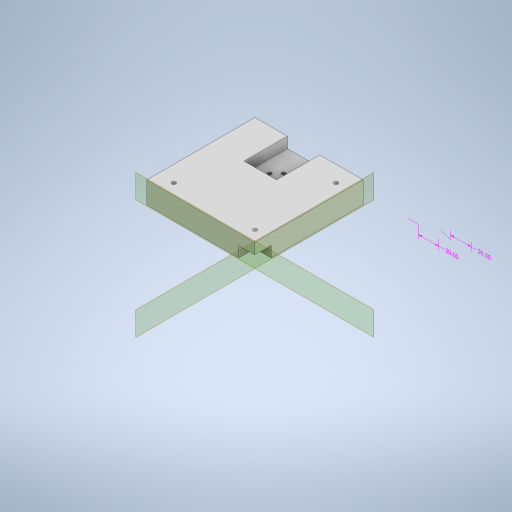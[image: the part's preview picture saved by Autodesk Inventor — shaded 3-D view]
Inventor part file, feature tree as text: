
AUTODESK INVENTOR PART (.ipt)
format: ipt  version: 2023 (Build 270158000, 158)  size: 370,176 bytes
history: native  units: mm
features: sketch x8, extrude x5, other x4, hole x3, plane x2, split x2
ambient origin geometry x8: Origin, YZ Plane, XZ Plane, XY Plane, X Axis, Y Axis, Z Axis, Center Point
bodies: Body1 (feature_tree)
feature tree (24):
  other  "Sólido1"
  other  "Anotaciones"
  extrude  "Extrusión1"  Depth=200.0mm
  extrude  "Extrusión2"  Depth=10.0mm TaperAngle=0.0deg
  extrude  "Extrusión3"  Depth=20.0mm
  hole  "Agujero1"  [1 undecoded]
  extrude  "Extrusión4"  Depth=10.0mm
  plane  "Plano de trabajo1"
  plane  "Plano de trabajo2"
  hole  "Agujero2"  [1 undecoded]
  extrude  "Extrusión5"  Depth=10.0mm TaperAngle=0.0deg
  hole  "Agujero3"  [1 undecoded]
  split  "Dividir1"
  split  "Dividir2"
  sketch  "Boceto1"  dims[d0=200.0mm d1=200.0mm]
  sketch  "Boceto2"  dims[d2=20.0mm d3=0.0mm]
  sketch  "Boceto3"  dims[d4=20.0mm d5=20.0mm d6=30.0mm d7=30.0mm d8=20.0mm d9=35.0mm d10=35.0mm d11=60.0mm d12=10.0mm d13=0.0mm]
  sketch  "Boceto4"  dims[d14=20.0mm d15=0.0mm]
  sketch  "Boceto5"  dims[d16=3.5mm d18=1.75mm d19=1.75mm d20=1.75mm d21=1.75mm d22=10.0mm d23=10.0mm d25=20.0mm]
  sketch  "Boceto7"  dims[d26=40.0mm d27=40.0mm]
  sketch  "Boceto8"  dims[d28=3.5mm d29=6.0mm d30=4.0mm d31=2.0mm d32=90.0deg d33=8.0mm d34=20.594885mm d38=10.0mm]
  sketch  "Boceto9"  dims[d39=10.0mm d40=40.0mm d41=10.0mm d42=0.0mm d52=3.5mm d54=10.0mm d55=10.0mm d56=3.5mm d57=6.0mm d58=4.0mm d59=2.0mm d60=90.0deg d61=8.0mm d62=20.594885mm d63=30.0mm d64=30.0mm d65=10.0mm d66=0.0mm d67=3.5mm d68=15.0mm d69=10.0mm d70=45.0deg d71=45.0deg d72=3.5mm d73=6.0mm d74=4.0mm d75=2.0mm d76=90.0deg d77=8.0mm d78=20.594885mm d43=6.672192mm d44=4.931866mm d45=30.0mm d46=5.890777mm d47=4.508932mm d48=30.0mm d83=0.5mm d84=0.872665mm d85=0.5mm d86=0.872665mm]
  other  "Cota lineal 1"
  other  "Cota lineal 2"
note: 3 required parameter values undecoded (feature->parameter linkage not recoverable at this tier; creation-order binding heuristic only, values carry confidence <= 0.55)
